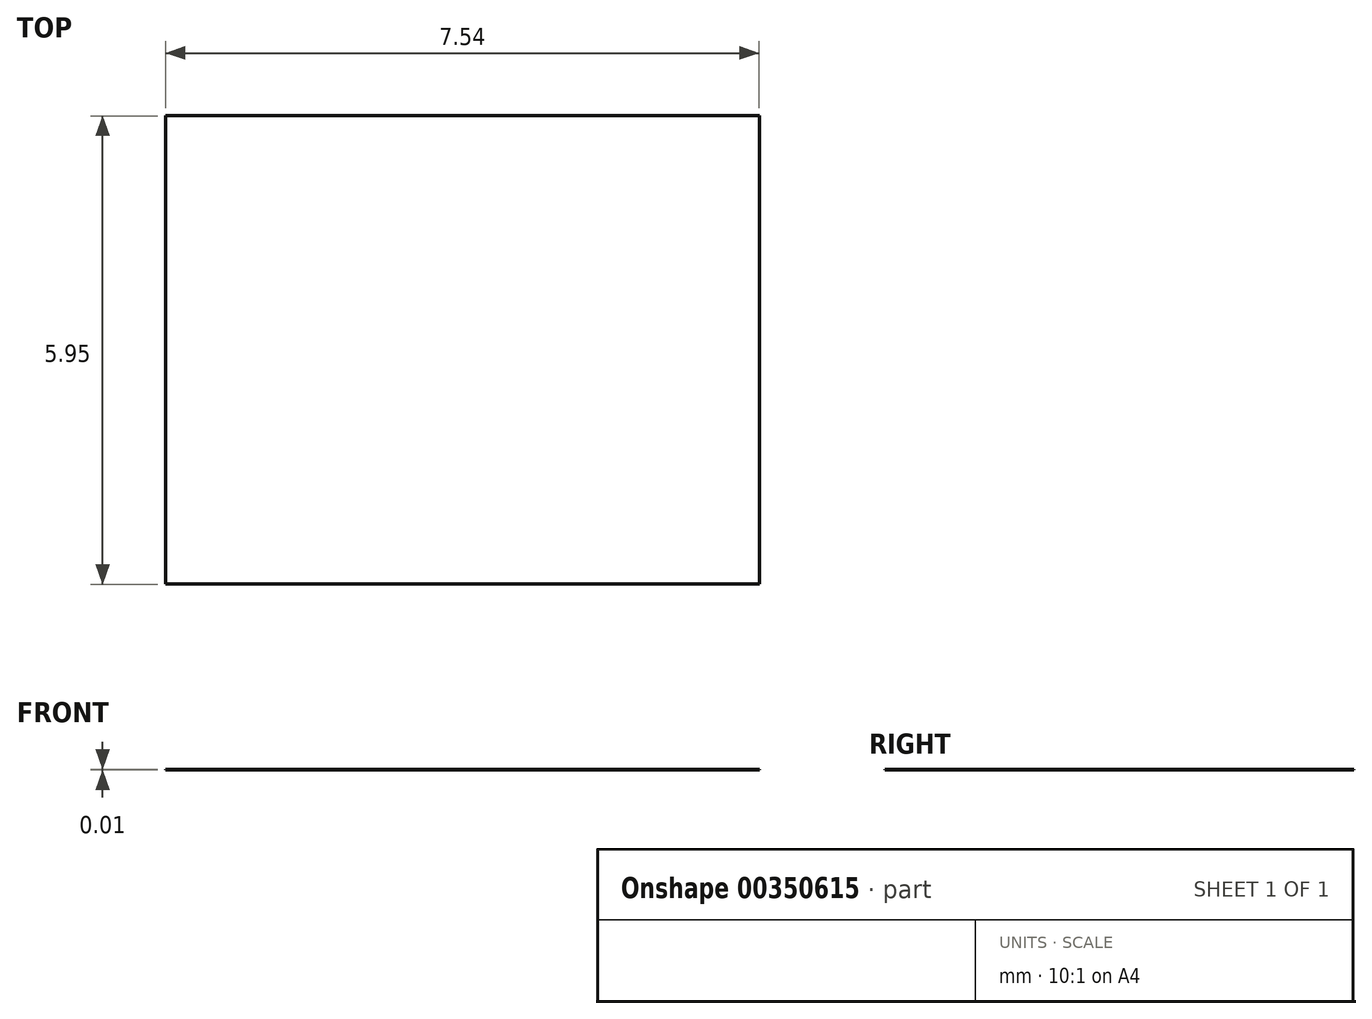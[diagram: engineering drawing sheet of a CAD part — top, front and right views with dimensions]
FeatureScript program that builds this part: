
annotation { "Feature Type Name" : "Feature", "Feature Type Description" : "" }
export const myFeature = defineFeature(function(context is Context, id is Id, definition is map)
    precondition{}
    {
        {
            var Q0;
            Q0=qCreatedBy(makeId("Top.planeOp"),FACE);
            var sketch = newSketch(context, id + "F0", { "sketchPlane" : qUnion([Q0])});
            skLineSegment(sketch, "E0.bottom", {"start": v(26.25, -17.74) * mm, "end": v(33.8, -17.74) * mm});
            skLineSegment(sketch, "E0.top", {"start": v(26.25, -23.69) * mm, "end": v(33.8, -23.69) * mm});
            skLineSegment(sketch, "E0.left", {"start": v(26.25, -17.74) * mm, "end": v(26.25, -23.69) * mm});
            skLineSegment(sketch, "E0.right", {"start": v(33.8, -17.74) * mm, "end": v(33.8, -23.69) * mm});
            skSolve(sketch);
        }
        {
            var Q0;
            Q0=makeQuery(id+"F0.imprint","IMPRINT",FACE,{"disambiguationData":[TD([[makeQuery(id+"F0.imprint","IMPRINT",EDGE,{"derivedFrom":sQuery(id+"F0.wireOp",EDGE,"E0.bottom")}),-1.0]])]});
            extrude(context, id + "F1", {"entities" : qUnion([Q0]), "depth" : 11 / 1625.6 * mm});
        }
    });
